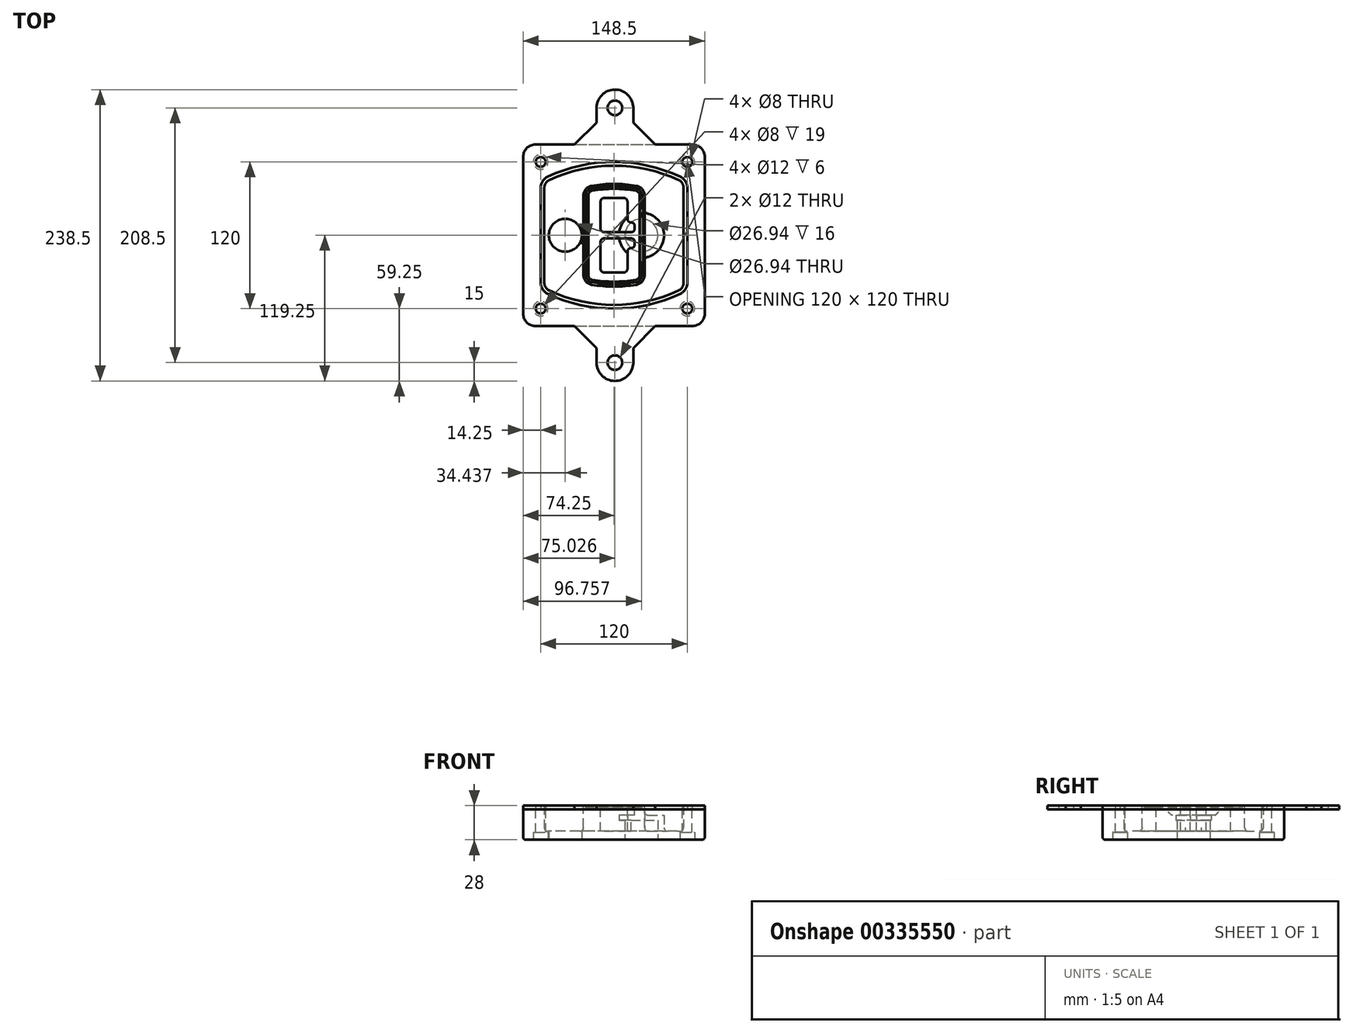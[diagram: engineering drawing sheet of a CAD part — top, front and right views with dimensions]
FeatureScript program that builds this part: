
annotation { "Feature Type Name" : "Feature", "Feature Type Description" : "" }
export const myFeature = defineFeature(function(context is Context, id is Id, definition is map)
    precondition{}
    {
        {
            var Q0;
            Q0=qCreatedBy(makeId("Top.planeOp"),FACE);
            var sketch = newSketch(context, id + "F0", { "sketchPlane" : qUnion([Q0])});
            skPoint(sketch, "E0.rect.middle", {"position": v(0, 0) * mm});
            skLineSegment(sketch, "E1.bottom", {"start": v(-64.25, -74.25) * mm, "end": v(64.25, -74.25) * mm});
            skLineSegment(sketch, "E1.top", {"start": v(-64.25, 74.25) * mm, "end": v(64.25, 74.25) * mm});
            skLineSegment(sketch, "E1.left", {"start": v(-74.25, -64.25) * mm, "end": v(-74.25, 64.25) * mm});
            skLineSegment(sketch, "E1.right", {"start": v(74.25, -64.25) * mm, "end": v(74.25, 64.25) * mm});
            skLineSegment(sketch, "E2", {"start": v(-74.25, 74.25) * mm, "end": v(74.25, -74.25) * mm, "construction": true});
            skLineSegment(sketch, "E3", {"start": v(74.25, 74.25) * mm, "end": v(-74.25, -74.25) * mm, "construction": true});
            skCircle(sketch, "E4", {"center": v(-60, 60) * mm, "radius": 4 * mm});
            skCircle(sketch, "E5", {"center": v(60, 60) * mm, "radius": 4 * mm});
            skCircle(sketch, "E6", {"center": v(60, -60) * mm, "radius": 4 * mm});
            skCircle(sketch, "E7", {"center": v(-60, -60) * mm, "radius": 4 * mm});
            skLineSegment(sketch, "E8", {"start": v(-60, 60) * mm, "end": v(60, 60) * mm, "construction": true});
            skLineSegment(sketch, "E9", {"start": v(60, 60) * mm, "end": v(60, -60) * mm, "construction": true});
            skLineSegment(sketch, "E10", {"start": v(60, -60) * mm, "end": v(-60, -60) * mm, "construction": true});
            skLineSegment(sketch, "E11", {"start": v(-60, -60) * mm, "end": v(-60, 60) * mm, "construction": true});
            skLineSegment(sketch, "E12", {"start": v(-60, 38.83) * mm, "end": v(-60, -38.83) * mm});
            skLineSegment(sketch, "E13", {"start": v(60, 38.83) * mm, "end": v(60, -38.83) * mm});
            skArc(sketch, "E14", {"start": v(54.26, 47.88) * mm, "mid": v(0, 60) * mm, "end": v(-54.26, 47.88) * mm});
            skArc(sketch, "E15", {"start": v(-54.26, -47.88) * mm, "mid": v(0, -60) * mm, "end": v(54.26, -47.88) * mm});
            skLineSegment(sketch, "E16", {"start": v(-60, 0) * mm, "end": v(60, 0) * mm, "construction": true});
            skPoint(sketch, "E17.visualSharp", {"position": v(-60, -45) * mm});
            skArc(sketch, "E17.filletArc", {"start": v(-60, -38.83) * mm, "mid": v(-58.44, -44.2) * mm, "end": v(-54.26, -47.88) * mm});
            skPoint(sketch, "E18.visualSharp", {"position": v(-60, 45) * mm});
            skArc(sketch, "E18.filletArc", {"start": v(-54.26, 47.88) * mm, "mid": v(-58.44, 44.2) * mm, "end": v(-60, 38.83) * mm});
            skPoint(sketch, "E19.visualSharp", {"position": v(60, 45) * mm});
            skArc(sketch, "E19.filletArc", {"start": v(60, 38.83) * mm, "mid": v(58.44, 44.2) * mm, "end": v(54.26, 47.88) * mm});
            skPoint(sketch, "E20.visualSharp", {"position": v(60, -45) * mm});
            skArc(sketch, "E20.filletArc", {"start": v(54.26, -47.88) * mm, "mid": v(58.44, -44.2) * mm, "end": v(60, -38.83) * mm});
            skPoint(sketch, "E21.visualSharp", {"position": v(-74.25, 74.25) * mm});
            skArc(sketch, "E21.filletArc", {"start": v(-64.25, 74.25) * mm, "mid": v(-71.32, 71.32) * mm, "end": v(-74.25, 64.25) * mm});
            skPoint(sketch, "E22.visualSharp", {"position": v(74.25, 74.25) * mm});
            skArc(sketch, "E22.filletArc", {"start": v(74.25, 64.25) * mm, "mid": v(71.32, 71.32) * mm, "end": v(64.25, 74.25) * mm});
            skPoint(sketch, "E23.visualSharp", {"position": v(74.25, -74.25) * mm});
            skArc(sketch, "E23.filletArc", {"start": v(64.25, -74.25) * mm, "mid": v(71.32, -71.32) * mm, "end": v(74.25, -64.25) * mm});
            skPoint(sketch, "E24.visualSharp", {"position": v(-74.25, -74.25) * mm});
            skArc(sketch, "E24.filletArc", {"start": v(-74.25, -64.25) * mm, "mid": v(-71.32, -71.32) * mm, "end": v(-64.25, -74.25) * mm});
            skArc(sketch, "E25.0", {"start": v(57, 38.83) * mm, "mid": v(55.9, 42.58) * mm, "end": v(52.98, 45.17) * mm});
            skLineSegment(sketch, "E25.1", {"start": v(57, 38.83) * mm, "end": v(57, -38.83) * mm});
            skArc(sketch, "E25.2", {"start": v(52.98, -45.17) * mm, "mid": v(55.9, -42.58) * mm, "end": v(57, -38.83) * mm});
            skArc(sketch, "E25.3", {"start": v(-52.98, -45.17) * mm, "mid": v(0, -57) * mm, "end": v(52.98, -45.17) * mm});
            skArc(sketch, "E25.4", {"start": v(-57, -38.83) * mm, "mid": v(-55.9, -42.58) * mm, "end": v(-52.98, -45.17) * mm});
            skArc(sketch, "E25.5", {"start": v(52.98, 45.17) * mm, "mid": v(0, 57) * mm, "end": v(-52.98, 45.17) * mm});
            skLineSegment(sketch, "E25.6", {"start": v(-57, 38.83) * mm, "end": v(-57, -38.83) * mm});
            skArc(sketch, "E25.7", {"start": v(-52.98, 45.17) * mm, "mid": v(-55.9, 42.58) * mm, "end": v(-57, 38.83) * mm});
            skArc(sketch, "E26.0", {"start": v(-55.96, 51.5) * mm, "mid": v(-61.82, 46.33) * mm, "end": v(-64, 38.83) * mm});
            skArc(sketch, "E26.1", {"start": v(55.96, 51.5) * mm, "mid": v(0, 64) * mm, "end": v(-55.96, 51.5) * mm});
            skArc(sketch, "E26.2", {"start": v(64, 38.83) * mm, "mid": v(61.82, 46.33) * mm, "end": v(55.96, 51.5) * mm});
            skLineSegment(sketch, "E26.3", {"start": v(64, 38.83) * mm, "end": v(64, -38.83) * mm});
            skArc(sketch, "E26.4", {"start": v(55.96, -51.5) * mm, "mid": v(61.82, -46.33) * mm, "end": v(64, -38.83) * mm});
            skLineSegment(sketch, "E26.5", {"start": v(-64, 38.83) * mm, "end": v(-64, -38.83) * mm});
            skArc(sketch, "E26.6", {"start": v(-55.96, -51.5) * mm, "mid": v(0, -64) * mm, "end": v(55.96, -51.5) * mm});
            skArc(sketch, "E26.7", {"start": v(-64, -38.83) * mm, "mid": v(-61.82, -46.33) * mm, "end": v(-55.96, -51.5) * mm});
            skSolve(sketch);
        }
        {
            var Q0;
            Q0=makeQuery(id+"F0.imprint","IMPRINT",FACE,{"disambiguationData":[TD([[makeQuery(id+"F0.imprint","IMPRINT",EDGE,{"derivedFrom":sQuery(id+"F0.wireOp",EDGE,"E1.bottom")}),1.0]])]});
            var Q1;
            Q1=makeQuery(id+"F0.imprint","IMPRINT",FACE,{"disambiguationData":[TD([[makeQuery(id+"F0.imprint","IMPRINT",EDGE,{"derivedFrom":sQuery(id+"F0.wireOp",EDGE,"E12")}),1.0]])]});
            var Q2;
            Q2=makeQuery(id+"F0.imprint","IMPRINT",FACE,{"disambiguationData":[TD([[makeQuery(id+"F0.imprint","IMPRINT",EDGE,{"derivedFrom":sQuery(id+"F0.wireOp",EDGE,"E25.0")}),1.0]])]});
            var Q3;
            Q3=makeQuery(id+"F0.imprint","IMPRINT",FACE,{"disambiguationData":[TD([[makeQuery(id+"F0.imprint","IMPRINT",EDGE,{"derivedFrom":sQuery(id+"F0.wireOp",EDGE,"E12")}),-1.0]])]});
            extrude(context, id + "F1", {"entities" : qUnion([Q0, Q1, Q2, Q3]), "oppositeDirection" : true, "depth" : 25 * mm});
        }
        {
            var Q0;
            Q0=makeQuery(id+"F0.imprint","IMPRINT",FACE,{"disambiguationData":[TD([[makeQuery(id+"F0.imprint","IMPRINT",EDGE,{"derivedFrom":sQuery(id+"F0.wireOp",EDGE,"E12")}),1.0]])]});
            extrude(context, id + "F2", {"entities" : qUnion([Q0]), "operationType" : NewBodyOperationType.ADD, "depth" : 3 * mm});
        }
        {
            var Q0;
            Q0=makeQuery(id+"F0.imprint","IMPRINT",FACE,{"disambiguationData":[TD([[makeQuery(id+"F0.imprint","IMPRINT",EDGE,{"derivedFrom":sQuery(id+"F0.wireOp",EDGE,"E25.0")}),1.0]])]});
            extrude(context, id + "F3", {"entities" : qUnion([Q0]), "operationType" : NewBodyOperationType.REMOVE, "oppositeDirection" : true, "depth" : 18 * mm});
        }
        {
            var Q0;
            Q0=makeQuery(id+"F2.opExtrude","CAP_FACE",FACE,{"disambiguationData":[OSD([sQuery(id+"F0.wireOp",EDGE,"E12"),sQuery(id+"F0.wireOp",EDGE,"E13"),sQuery(id+"F0.wireOp",EDGE,"E14"),sQuery(id+"F0.wireOp",EDGE,"E15"),sQuery(id+"F0.wireOp",EDGE,"E17.filletArc"),sQuery(id+"F0.wireOp",EDGE,"E18.filletArc"),sQuery(id+"F0.wireOp",EDGE,"E19.filletArc"),sQuery(id+"F0.wireOp",EDGE,"E20.filletArc"),sQuery(id+"F0.wireOp",EDGE,"E25.0"),sQuery(id+"F0.wireOp",EDGE,"E25.1"),sQuery(id+"F0.wireOp",EDGE,"E25.2"),sQuery(id+"F0.wireOp",EDGE,"E25.3"),sQuery(id+"F0.wireOp",EDGE,"E25.4"),sQuery(id+"F0.wireOp",EDGE,"E25.5"),sQuery(id+"F0.wireOp",EDGE,"E25.6"),sQuery(id+"F0.wireOp",EDGE,"E25.7")])],"isStart":false});
            var sketch = newSketch(context, id + "F4", { "sketchPlane" : qUnion([Q0])});
            skArc(sketch, "E27.0", {"start": v(-18.34, -40.45) * mm, "mid": v(0, -42) * mm, "end": v(18.34, -40.45) * mm});
            skArc(sketch, "E28.0", {"start": v(18.34, 40.45) * mm, "mid": v(0, 42) * mm, "end": v(-18.34, 40.45) * mm});
            skLineSegment(sketch, "E29", {"start": v(-25, 32.57) * mm, "end": v(-25, -32.57) * mm});
            skLineSegment(sketch, "E30", {"start": v(25, 32.57) * mm, "end": v(25, -32.57) * mm});
            skLineSegment(sketch, "E31", {"start": v(-25, 39.1) * mm, "end": v(25, 39.1) * mm, "construction": true});
            skLineSegment(sketch, "E32", {"start": v(-25, -39.1) * mm, "end": v(25, -39.1) * mm, "construction": true});
            skPoint(sketch, "E33.visualSharp", {"position": v(-25, 39.1) * mm});
            skArc(sketch, "E33.filletArc", {"start": v(-18.34, 40.45) * mm, "mid": v(-23.11, 37.73) * mm, "end": v(-25, 32.57) * mm});
            skPoint(sketch, "E34.visualSharp", {"position": v(25, 39.1) * mm});
            skArc(sketch, "E34.filletArc", {"start": v(25, 32.57) * mm, "mid": v(23.11, 37.73) * mm, "end": v(18.34, 40.45) * mm});
            skPoint(sketch, "E35.visualSharp", {"position": v(25, -39.1) * mm});
            skArc(sketch, "E35.filletArc", {"start": v(18.34, -40.45) * mm, "mid": v(23.11, -37.73) * mm, "end": v(25, -32.57) * mm});
            skPoint(sketch, "E36.visualSharp", {"position": v(-25, -39.1) * mm});
            skArc(sketch, "E36.filletArc", {"start": v(-25, -32.57) * mm, "mid": v(-23.11, -37.73) * mm, "end": v(-18.34, -40.45) * mm});
            skArc(sketch, "E37.0", {"start": v(52.98, 45.17) * mm, "mid": v(0, 57) * mm, "end": v(-52.98, 45.17) * mm});
            skArc(sketch, "E37.1", {"start": v(-52.98, 45.17) * mm, "mid": v(-55.9, 42.58) * mm, "end": v(-57, 38.83) * mm});
            skLineSegment(sketch, "E37.2", {"start": v(-57, 38.83) * mm, "end": v(-57, -38.83) * mm});
            skArc(sketch, "E37.3", {"start": v(-57, -38.83) * mm, "mid": v(-55.9, -42.58) * mm, "end": v(-52.98, -45.17) * mm});
            skArc(sketch, "E37.4", {"start": v(-52.98, -45.17) * mm, "mid": v(0, -57) * mm, "end": v(52.98, -45.17) * mm});
            skArc(sketch, "E37.5", {"start": v(52.98, -45.17) * mm, "mid": v(55.9, -42.58) * mm, "end": v(57, -38.83) * mm});
            skLineSegment(sketch, "E37.6", {"start": v(57, 38.83) * mm, "end": v(57, -38.83) * mm});
            skArc(sketch, "E37.7", {"start": v(57, 38.83) * mm, "mid": v(55.9, 42.58) * mm, "end": v(52.98, 45.17) * mm});
            skLineSegment(sketch, "E38.0", {"start": v(23, 32.57) * mm, "end": v(23, -32.57) * mm});
            skArc(sketch, "E38.1", {"start": v(18, -38.48) * mm, "mid": v(21.58, -36.44) * mm, "end": v(23, -32.57) * mm});
            skArc(sketch, "E38.2", {"start": v(-18, -38.48) * mm, "mid": v(0, -40) * mm, "end": v(18, -38.48) * mm});
            skArc(sketch, "E38.3", {"start": v(-23, -32.57) * mm, "mid": v(-21.58, -36.44) * mm, "end": v(-18, -38.48) * mm});
            skLineSegment(sketch, "E38.4", {"start": v(-23, 32.57) * mm, "end": v(-23, -32.57) * mm});
            skArc(sketch, "E38.5", {"start": v(23, 32.57) * mm, "mid": v(21.58, 36.44) * mm, "end": v(18, 38.48) * mm});
            skArc(sketch, "E38.6", {"start": v(-18, 38.48) * mm, "mid": v(-21.58, 36.44) * mm, "end": v(-23, 32.57) * mm});
            skArc(sketch, "E38.7", {"start": v(18, 38.48) * mm, "mid": v(0, 40) * mm, "end": v(-18, 38.48) * mm});
            skArc(sketch, "E39.0", {"start": v(21, 32.57) * mm, "mid": v(20.06, 35.15) * mm, "end": v(17.67, 36.5) * mm});
            skLineSegment(sketch, "E39.1", {"start": v(21, 32.57) * mm, "end": v(21, -32.57) * mm});
            skArc(sketch, "E39.2", {"start": v(17.67, -36.5) * mm, "mid": v(20.06, -35.15) * mm, "end": v(21, -32.57) * mm});
            skArc(sketch, "E39.3", {"start": v(-17.67, -36.5) * mm, "mid": v(0, -38) * mm, "end": v(17.67, -36.5) * mm});
            skArc(sketch, "E39.4", {"start": v(-21, -32.57) * mm, "mid": v(-20.06, -35.15) * mm, "end": v(-17.67, -36.5) * mm});
            skArc(sketch, "E39.5", {"start": v(17.67, 36.5) * mm, "mid": v(0, 38) * mm, "end": v(-17.67, 36.5) * mm});
            skLineSegment(sketch, "E39.6", {"start": v(-21, 32.57) * mm, "end": v(-21, -32.57) * mm});
            skArc(sketch, "E39.7", {"start": v(-17.67, 36.5) * mm, "mid": v(-20.06, 35.15) * mm, "end": v(-21, 32.57) * mm});
            skLineSegment(sketch, "E40", {"start": v(-25, 0) * mm, "end": v(25, 0) * mm, "construction": true});
            skLineSegment(sketch, "E41", {"start": v(-11, 5.5) * mm, "end": v(-11, 27.5) * mm});
            skLineSegment(sketch, "E42", {"start": v(-8, 30.5) * mm, "end": v(8, 30.5) * mm});
            skLineSegment(sketch, "E43", {"start": v(11, 27.5) * mm, "end": v(11, 13.5) * mm});
            skLineSegment(sketch, "E44", {"start": v(14, 10.5) * mm, "end": v(14, 10.5) * mm});
            skLineSegment(sketch, "E45", {"start": v(17, 7.5) * mm, "end": v(17, 5.5) * mm});
            skLineSegment(sketch, "E46", {"start": v(14, 2.5) * mm, "end": v(-8, 2.5) * mm});
            skPoint(sketch, "E47.visualSharp", {"position": v(-11, 30.5) * mm});
            skArc(sketch, "E47.filletArc", {"start": v(-8, 30.5) * mm, "mid": v(-10.12, 29.62) * mm, "end": v(-11, 27.5) * mm});
            skPoint(sketch, "E48.visualSharp", {"position": v(11, 30.5) * mm});
            skArc(sketch, "E48.filletArc", {"start": v(11, 27.5) * mm, "mid": v(10.12, 29.62) * mm, "end": v(8, 30.5) * mm});
            skPoint(sketch, "E49.visualSharp", {"position": v(11, 10.5) * mm});
            skArc(sketch, "E49.filletArc", {"start": v(11, 13.5) * mm, "mid": v(11.88, 11.38) * mm, "end": v(14, 10.5) * mm});
            skPoint(sketch, "E50.visualSharp", {"position": v(17, 10.5) * mm});
            skArc(sketch, "E50.filletArc", {"start": v(17, 7.5) * mm, "mid": v(16.12, 9.62) * mm, "end": v(14, 10.5) * mm});
            skPoint(sketch, "E51.visualSharp", {"position": v(17, 2.5) * mm});
            skArc(sketch, "E51.filletArc", {"start": v(14, 2.5) * mm, "mid": v(16.12, 3.38) * mm, "end": v(17, 5.5) * mm});
            skPoint(sketch, "E52.visualSharp", {"position": v(-11, 2.5) * mm});
            skArc(sketch, "E52.filletArc", {"start": v(-11, 5.5) * mm, "mid": v(-10.12, 3.38) * mm, "end": v(-8, 2.5) * mm});
            skLineSegment(sketch, "E53.0.MirrorCS", {"start": v(14, -2.5) * mm, "end": v(-8, -2.5) * mm});
            skArc(sketch, "E54.0.MirrorCS", {"start": v(-11, -5.5) * mm, "mid": v(-10.12, -3.38) * mm, "end": v(-8, -2.5) * mm});
            skLineSegment(sketch, "E55.0.MirrorCS", {"start": v(-11, -5.5) * mm, "end": v(-11, -27.5) * mm});
            skArc(sketch, "E56.0.MirrorCS", {"start": v(-8, -30.5) * mm, "mid": v(-10.12, -29.62) * mm, "end": v(-11, -27.5) * mm});
            skLineSegment(sketch, "E57.0.MirrorCS", {"start": v(-8, -30.5) * mm, "end": v(8, -30.5) * mm});
            skArc(sketch, "E58.0.MirrorCS", {"start": v(11, -27.5) * mm, "mid": v(10.12, -29.62) * mm, "end": v(8, -30.5) * mm});
            skLineSegment(sketch, "E59.0.MirrorCS", {"start": v(11, -27.5) * mm, "end": v(11, -13.5) * mm});
            skArc(sketch, "E60.0.MirrorCS", {"start": v(11, -13.5) * mm, "mid": v(11.88, -11.38) * mm, "end": v(14, -10.5) * mm});
            skArc(sketch, "E61.0.MirrorCS", {"start": v(17, -7.5) * mm, "mid": v(16.12, -9.62) * mm, "end": v(14, -10.5) * mm});
            skLineSegment(sketch, "E62.0.MirrorCS", {"start": v(17, -7.5) * mm, "end": v(17, -5.5) * mm});
            skArc(sketch, "E63.0.MirrorCS", {"start": v(14, -2.5) * mm, "mid": v(16.12, -3.38) * mm, "end": v(17, -5.5) * mm});
            skSolve(sketch);
        }
        {
            var Q0;
            Q0=makeQuery(id+"F4.imprint","IMPRINT",FACE,{"disambiguationData":[TD([[makeQuery(id+"F4.imprint","IMPRINT",EDGE,{"derivedFrom":sQuery(id+"F4.wireOp",EDGE,"E27.0")}),1.0]])]});
            var Q1;
            Q1=makeQuery(id+"F4.imprint","IMPRINT",FACE,{"disambiguationData":[TD([[makeQuery(id+"F4.imprint","IMPRINT",EDGE,{"derivedFrom":sQuery(id+"F4.wireOp",EDGE,"E38.0")}),-1.0]])]});
            var Q2;
            Q2=makeQuery(id+"F4.imprint","IMPRINT",FACE,{"disambiguationData":[TD([[makeQuery(id+"F4.imprint","IMPRINT",EDGE,{"derivedFrom":sQuery(id+"F4.wireOp",EDGE,"E39.0")}),1.0]])]});
            extrude(context, id + "F5", {"entities" : qUnion([Q0, Q1, Q2]), "operationType" : NewBodyOperationType.ADD, "endBound" : BoundingType.UP_TO_NEXT, "oppositeDirection" : true, "depth" : 25 * mm});
        }
        {
            var Q0;
            Q0=makeQuery(id+"F4.imprint","IMPRINT",FACE,{"disambiguationData":[TD([[makeQuery(id+"F4.imprint","IMPRINT",EDGE,{"derivedFrom":sQuery(id+"F4.wireOp",EDGE,"E38.0")}),-1.0]])]});
            extrude(context, id + "F6", {"entities" : qUnion([Q0]), "operationType" : NewBodyOperationType.REMOVE, "oppositeDirection" : true, "depth" : 2 * mm});
        }
        {
            var Q0;
            Q0=makeQuery(id+"F1.opExtrude","CAP_FACE",FACE,{"disambiguationData":[OSD([sQuery(id+"F0.wireOp",EDGE,"E1.bottom"),sQuery(id+"F0.wireOp",EDGE,"E1.top"),sQuery(id+"F0.wireOp",EDGE,"E1.left"),sQuery(id+"F0.wireOp",EDGE,"E1.right"),sQuery(id+"F0.wireOp",EDGE,"E4"),sQuery(id+"F0.wireOp",EDGE,"E5"),sQuery(id+"F0.wireOp",EDGE,"E6"),sQuery(id+"F0.wireOp",EDGE,"E7"),sQuery(id+"F0.wireOp",EDGE,"E21.filletArc"),sQuery(id+"F0.wireOp",EDGE,"E22.filletArc"),sQuery(id+"F0.wireOp",EDGE,"E23.filletArc"),sQuery(id+"F0.wireOp",EDGE,"E24.filletArc")])],"isStart":false});
            var sketch = newSketch(context, id + "F7", { "sketchPlane" : qUnion([Q0])});
            skCircle(sketch, "E64", {"center": v(22.5, 0) * mm, "radius": 13.47 * mm});
            skCircle(sketch, "E65", {"center": v(-39.81, 0) * mm, "radius": 13.47 * mm});
            skLineSegment(sketch, "E66", {"start": v(74.25, 0) * mm, "end": v(-74.25, 0) * mm});
            skCircle(sketch, "E67", {"center": v(22.5, 0) * mm, "radius": 18.47 * mm});
            skCircle(sketch, "E68", {"center": v(60, -60) * mm, "radius": 6 * mm});
            skCircle(sketch, "E69", {"center": v(-60, -60) * mm, "radius": 6 * mm});
            skCircle(sketch, "E70", {"center": v(-60, 60) * mm, "radius": 6 * mm});
            skCircle(sketch, "E71", {"center": v(60, 60) * mm, "radius": 6 * mm});
            skSolve(sketch);
        }
        {
            var Q0;
            {var subQ1=sQuery(id+"F7.wireOp",EDGE,"E66");var subQ4=sQuery(id+"F7.wireOp",EDGE,"E64");var subQ6=makeQuery(id+"F7.imprint","INTERSECT",VERTEX,{"disambiguationData":[OD(0.0)],"derivedFrom":[subQ4,subQ1]});Q0=makeQuery(id+"F7.imprint","IMPRINT",FACE,{"disambiguationData":[TD([[makeQuery(id+"F7.imprint","IMPRINT",EDGE,{"disambiguationData":[TD([[subQ6,-1.0]])],"derivedFrom":subQ4}),-1.0]])]});}
            var Q1;
            {var subQ0=sQuery(id+"F7.wireOp",EDGE,"E66");var subQ1=sQuery(id+"F7.wireOp",EDGE,"E64");var subQ3=makeQuery(id+"F7.imprint","INTERSECT",VERTEX,{"disambiguationData":[OD(0.0)],"derivedFrom":[subQ1,subQ0]});Q1=makeQuery(id+"F7.imprint","IMPRINT",FACE,{"disambiguationData":[TD([[makeQuery(id+"F7.imprint","IMPRINT",EDGE,{"disambiguationData":[TD([[subQ3,-1.0]])],"derivedFrom":subQ1}),1.0]])]});}
            var Q2;
            {var subQ0=sQuery(id+"F7.wireOp",EDGE,"E66");var subQ1=sQuery(id+"F7.wireOp",EDGE,"E64");var subQ3=makeQuery(id+"F7.imprint","INTERSECT",VERTEX,{"disambiguationData":[OD(0.0)],"derivedFrom":[subQ1,subQ0]});Q2=makeQuery(id+"F7.imprint","IMPRINT",FACE,{"disambiguationData":[TD([[makeQuery(id+"F7.imprint","IMPRINT",EDGE,{"disambiguationData":[TD([[subQ3,1.0]])],"derivedFrom":subQ1}),1.0]])]});}
            var Q3;
            {var subQ1=sQuery(id+"F7.wireOp",EDGE,"E66");var subQ4=sQuery(id+"F7.wireOp",EDGE,"E64");var subQ6=makeQuery(id+"F7.imprint","INTERSECT",VERTEX,{"disambiguationData":[OD(0.0)],"derivedFrom":[subQ4,subQ1]});Q3=makeQuery(id+"F7.imprint","IMPRINT",FACE,{"disambiguationData":[TD([[makeQuery(id+"F7.imprint","IMPRINT",EDGE,{"disambiguationData":[TD([[subQ6,1.0]])],"derivedFrom":subQ4}),-1.0]])]});}
            extrude(context, id + "F8", {"entities" : qUnion([Q0, Q1, Q2, Q3]), "operationType" : NewBodyOperationType.ADD, "oppositeDirection" : true, "depth" : 20 * mm});
        }
        {
            var Q0;
            {var subQ0=sQuery(id+"F7.wireOp",EDGE,"E66");var subQ1=sQuery(id+"F7.wireOp",EDGE,"E64");var subQ3=makeQuery(id+"F7.imprint","INTERSECT",VERTEX,{"disambiguationData":[OD(0.0)],"derivedFrom":[subQ1,subQ0]});Q0=makeQuery(id+"F7.imprint","IMPRINT",FACE,{"disambiguationData":[TD([[makeQuery(id+"F7.imprint","IMPRINT",EDGE,{"disambiguationData":[TD([[subQ3,-1.0]])],"derivedFrom":subQ1}),1.0]])]});}
            var Q1;
            {var subQ0=sQuery(id+"F7.wireOp",EDGE,"E66");var subQ1=sQuery(id+"F7.wireOp",EDGE,"E64");var subQ3=makeQuery(id+"F7.imprint","INTERSECT",VERTEX,{"disambiguationData":[OD(0.0)],"derivedFrom":[subQ1,subQ0]});Q1=makeQuery(id+"F7.imprint","IMPRINT",FACE,{"disambiguationData":[TD([[makeQuery(id+"F7.imprint","IMPRINT",EDGE,{"disambiguationData":[TD([[subQ3,1.0]])],"derivedFrom":subQ1}),1.0]])]});}
            extrude(context, id + "F9", {"entities" : qUnion([Q0, Q1]), "operationType" : NewBodyOperationType.REMOVE, "oppositeDirection" : true, "depth" : 16 * mm});
        }
        {
            var Q0;
            {var subQ0=sQuery(id+"F7.wireOp",EDGE,"E66");var subQ1=sQuery(id+"F7.wireOp",EDGE,"E65");var subQ3=makeQuery(id+"F7.imprint","INTERSECT",VERTEX,{"disambiguationData":[OD(0.0)],"derivedFrom":[subQ1,subQ0]});Q0=makeQuery(id+"F7.imprint","IMPRINT",FACE,{"disambiguationData":[TD([[makeQuery(id+"F7.imprint","IMPRINT",EDGE,{"disambiguationData":[TD([[subQ3,-1.0]])],"derivedFrom":subQ1}),1.0]])]});}
            var Q1;
            {var subQ0=sQuery(id+"F7.wireOp",EDGE,"E66");var subQ1=sQuery(id+"F7.wireOp",EDGE,"E65");var subQ3=makeQuery(id+"F7.imprint","INTERSECT",VERTEX,{"disambiguationData":[OD(0.0)],"derivedFrom":[subQ1,subQ0]});Q1=makeQuery(id+"F7.imprint","IMPRINT",FACE,{"disambiguationData":[TD([[makeQuery(id+"F7.imprint","IMPRINT",EDGE,{"disambiguationData":[TD([[subQ3,1.0]])],"derivedFrom":subQ1}),1.0]])]});}
            extrude(context, id + "F10", {"entities" : qUnion([Q0, Q1]), "operationType" : NewBodyOperationType.REMOVE, "oppositeDirection" : true, "depth" : 25 * mm});
        }
        {
            var Q0;
            Q0=makeQuery(id+"F7.imprint","IMPRINT",FACE,{"disambiguationData":[TD([[makeQuery(id+"F7.imprint","IMPRINT",EDGE,{"derivedFrom":sQuery(id+"F7.wireOp",EDGE,"E68")}),1.0]])]});
            var Q1;
            Q1=makeQuery(id+"F7.imprint","IMPRINT",FACE,{"disambiguationData":[TD([[makeQuery(id+"F7.imprint","IMPRINT",EDGE,{"derivedFrom":makeQuery(id+"F1.opExtrude","CAP_EDGE",EDGE,{"disambiguationData":[OSD([sQuery(id+"F0.wireOp",EDGE,"E5")])],"isStart":false})}),-1.0]])]});
            var Q2;
            Q2=makeQuery(id+"F7.imprint","IMPRINT",FACE,{"disambiguationData":[TD([[makeQuery(id+"F7.imprint","IMPRINT",EDGE,{"derivedFrom":sQuery(id+"F7.wireOp",EDGE,"E69")}),1.0]])]});
            var Q3;
            Q3=makeQuery(id+"F7.imprint","IMPRINT",FACE,{"disambiguationData":[TD([[makeQuery(id+"F7.imprint","IMPRINT",EDGE,{"derivedFrom":makeQuery(id+"F1.opExtrude","CAP_EDGE",EDGE,{"disambiguationData":[OSD([sQuery(id+"F0.wireOp",EDGE,"E4")])],"isStart":false})}),-1.0]])]});
            var Q4;
            Q4=makeQuery(id+"F7.imprint","IMPRINT",FACE,{"disambiguationData":[TD([[makeQuery(id+"F7.imprint","IMPRINT",EDGE,{"derivedFrom":sQuery(id+"F7.wireOp",EDGE,"E70")}),1.0]])]});
            var Q5;
            Q5=makeQuery(id+"F7.imprint","IMPRINT",FACE,{"disambiguationData":[TD([[makeQuery(id+"F7.imprint","IMPRINT",EDGE,{"derivedFrom":makeQuery(id+"F1.opExtrude","CAP_EDGE",EDGE,{"disambiguationData":[OSD([sQuery(id+"F0.wireOp",EDGE,"E7")])],"isStart":false})}),-1.0]])]});
            var Q6;
            Q6=makeQuery(id+"F7.imprint","IMPRINT",FACE,{"disambiguationData":[TD([[makeQuery(id+"F7.imprint","IMPRINT",EDGE,{"derivedFrom":sQuery(id+"F7.wireOp",EDGE,"E71")}),1.0]])]});
            var Q7;
            Q7=makeQuery(id+"F7.imprint","IMPRINT",FACE,{"disambiguationData":[TD([[makeQuery(id+"F7.imprint","IMPRINT",EDGE,{"derivedFrom":makeQuery(id+"F1.opExtrude","CAP_EDGE",EDGE,{"disambiguationData":[OSD([sQuery(id+"F0.wireOp",EDGE,"E6")])],"isStart":false})}),-1.0]])]});
            extrude(context, id + "F11", {"entities" : qUnion([Q0, Q1, Q2, Q3, Q4, Q5, Q6, Q7]), "operationType" : NewBodyOperationType.REMOVE, "oppositeDirection" : true, "depth" : 6 * mm});
        }
        {
            var Q0;
            Q0=makeQuery(id+"F9.boolean.opBoolean","COPY",FACE,{"derivedFrom":makeQuery(id+"F9.opExtrude","CAP_FACE",FACE,{"disambiguationData":[OSD([sQuery(id+"F7.wireOp",EDGE,"E64")])],"isStart":false})});
            var sketch = newSketch(context, id + "F12", { "sketchPlane" : qUnion([Q0])});
            skArc(sketch, "E72.0", {"start": v(11, 14.45) * mm, "mid": v(6.45, 9.13) * mm, "end": v(4.2, 2.5) * mm});
            skArc(sketch, "E72.1", {"start": v(4.2, -2.5) * mm, "mid": v(6.45, -9.13) * mm, "end": v(11, -14.45) * mm});
            skLineSegment(sketch, "E73", {"start": v(4.2, -2.5) * mm, "end": v(14, -2.5) * mm});
            skLineSegment(sketch, "E74.0", {"start": v(14, 2.5) * mm, "end": v(4.2, 2.5) * mm});
            skArc(sketch, "E74.1", {"start": v(14, 2.5) * mm, "mid": v(16.12, 3.38) * mm, "end": v(17, 5.5) * mm});
            skLineSegment(sketch, "E74.2", {"start": v(17, 7.5) * mm, "end": v(17, 5.5) * mm});
            skArc(sketch, "E74.3", {"start": v(17, 7.5) * mm, "mid": v(16.12, 9.62) * mm, "end": v(14, 10.5) * mm});
            skArc(sketch, "E74.4", {"start": v(11, 13.5) * mm, "mid": v(11.88, 11.38) * mm, "end": v(14, 10.5) * mm});
            skLineSegment(sketch, "E74.5", {"start": v(11, 14.45) * mm, "end": v(11, 13.5) * mm});
            skLineSegment(sketch, "E74.7", {"start": v(14, -2.5) * mm, "end": v(4.2, -2.5) * mm});
            skArc(sketch, "E74.8", {"start": v(14, -2.5) * mm, "mid": v(16.12, -3.38) * mm, "end": v(17, -5.5) * mm});
            skLineSegment(sketch, "E74.9", {"start": v(17, -7.5) * mm, "end": v(17, -5.5) * mm});
            skArc(sketch, "E74.10", {"start": v(17, -7.5) * mm, "mid": v(16.12, -9.62) * mm, "end": v(14, -10.5) * mm});
            skArc(sketch, "E74.11", {"start": v(11, -13.5) * mm, "mid": v(11.88, -11.38) * mm, "end": v(14, -10.5) * mm});
            skLineSegment(sketch, "E74.12", {"start": v(11, -14.45) * mm, "end": v(11, -13.5) * mm});
            skPoint(sketch, "E75.orphan", {"position": v(11, -27.5) * mm});
            skPoint(sketch, "E76.orphan", {"position": v(-8, -2.5) * mm});
            skPoint(sketch, "E77.orphan", {"position": v(-8, 2.5) * mm});
            skPoint(sketch, "E78.orphan", {"position": v(11, 27.5) * mm});
            skSolve(sketch);
        }
        {
            var Q0;
            {var subQ7=sQuery(id+"F12.wireOp",EDGE,"E72.0");var subQ14=sQuery(id+"F12.wireOp",EDGE,"E72.1");var subQ16=sQuery(id+"F12.wireOp",EDGE,"E74.1");var subQ18=sQuery(id+"F12.wireOp",EDGE,"E74.8");Q0=qUnion([makeQuery(id+"F12.imprint","IMPRINT",FACE,{"disambiguationData":[TD([[makeQuery(id+"F12.imprint","IMPRINT",EDGE,{"derivedFrom":subQ7}),1.0]])]}),makeQuery(id+"F12.imprint","IMPRINT",FACE,{"disambiguationData":[TD([[makeQuery(id+"F12.imprint","IMPRINT",EDGE,{"derivedFrom":subQ14}),1.0]])]}),makeQuery(id+"F12.imprint","IMPRINT",FACE,{"disambiguationData":[TD([[makeQuery(id+"F12.imprint","IMPRINT",EDGE,{"derivedFrom":subQ16}),1.0]])]}),makeQuery(id+"F12.imprint","IMPRINT",FACE,{"disambiguationData":[TD([[makeQuery(id+"F12.imprint","IMPRINT",EDGE,{"derivedFrom":subQ18}),-1.0]])]})]);}
            var Q1;
            Q1=makeQuery(id+"F5.boolean.opBoolean","SPLIT",FACE,{"disambiguationData":[TD([makeQuery(id+"F5.opExtrude","SWEPT_FACE",FACE,{"disambiguationData":[OSD([sQuery(id+"F4.wireOp",EDGE,"E41")])]})])],"derivedFrom":makeQuery(id+"F3.boolean.opBoolean","COPY",FACE,{"derivedFrom":makeQuery(id+"F3.opExtrude","CAP_FACE",FACE,{"disambiguationData":[OSD([sQuery(id+"F0.wireOp",EDGE,"E25.0"),sQuery(id+"F0.wireOp",EDGE,"E25.1"),sQuery(id+"F0.wireOp",EDGE,"E25.2"),sQuery(id+"F0.wireOp",EDGE,"E25.3"),sQuery(id+"F0.wireOp",EDGE,"E25.4"),sQuery(id+"F0.wireOp",EDGE,"E25.5"),sQuery(id+"F0.wireOp",EDGE,"E25.6"),sQuery(id+"F0.wireOp",EDGE,"E25.7")])],"isStart":false})})});
            extrude(context, id + "F13", {"entities" : qUnion([Q0]), "operationType" : NewBodyOperationType.REMOVE, "endBound" : BoundingType.UP_TO_SURFACE, "endBoundEntityFace" : qUnion([Q1]), "depth" : 25 * mm});
        }
        {
            var Q0;
            Q0=makeQuery(id+"F3.boolean.opBoolean","COPY",EDGE,{"derivedFrom":makeQuery(id+"F3.opExtrude","CAP_EDGE",EDGE,{"disambiguationData":[OSD([sQuery(id+"F0.wireOp",EDGE,"E25.6")])],"isStart":false})});
            var Q1;
            Q1=makeQuery(id+"F8.boolean.opBoolean","INTERSECT",EDGE,{"derivedFrom":[makeQuery(id+"F5.opExtrude","SWEPT_FACE",FACE,{"disambiguationData":[OSD([sQuery(id+"F4.wireOp",EDGE,"E30")])]}),makeQuery(id+"F8.opExtrude","CAP_FACE",FACE,{"disambiguationData":[OSD([sQuery(id+"F7.wireOp",EDGE,"E67")])],"isStart":false})]});
            var Q2;
            Q2=makeQuery(id+"F8.boolean.opBoolean","INTERSECT",EDGE,{"disambiguationData":[OD(1.0)],"derivedFrom":[makeQuery(id+"F5.opExtrude","SWEPT_FACE",FACE,{"disambiguationData":[OSD([sQuery(id+"F4.wireOp",EDGE,"E30")])]}),makeQuery(id+"F8.opExtrude","SWEPT_FACE",FACE,{"disambiguationData":[OSD([sQuery(id+"F7.wireOp",EDGE,"E67")])]})]});
            var Q3;
            {var subQ0=sQuery(id+"F4.wireOp",EDGE,"E30");Q3=makeQuery(id+"F8.boolean.opBoolean","SPLIT",EDGE,{"disambiguationData":[TD([makeQuery(id+"F5.opExtrude","SWEPT_FACE",FACE,{"disambiguationData":[OSD([sQuery(id+"F4.wireOp",EDGE,"E35.filletArc")])]})])],"derivedFrom":makeQuery(id+"F5.opExtrude","CAP_EDGE",EDGE,{"disambiguationData":[OSD([subQ0])],"isStart":false})});}
            var Q4;
            {var subQ0=sQuery(id+"F0.wireOp",EDGE,"E25.7");var subQ1=sQuery(id+"F0.wireOp",EDGE,"E25.1");var subQ2=sQuery(id+"F0.wireOp",EDGE,"E25.6");var subQ3=sQuery(id+"F0.wireOp",EDGE,"E25.5");var subQ4=sQuery(id+"F0.wireOp",EDGE,"E25.4");var subQ5=sQuery(id+"F0.wireOp",EDGE,"E25.0");var subQ6=sQuery(id+"F0.wireOp",EDGE,"E25.2");var subQ7=sQuery(id+"F0.wireOp",EDGE,"E25.3");Q4=makeQuery(id+"F8.boolean.opBoolean","INTERSECT",EDGE,{"derivedFrom":[makeQuery(id+"F5.boolean.opBoolean","SPLIT",FACE,{"disambiguationData":[TD([makeQuery(id+"F2.opExtrude","SWEPT_FACE",FACE,{"disambiguationData":[OSD([subQ5])]})])],"derivedFrom":makeQuery(id+"F3.boolean.opBoolean","COPY",FACE,{"derivedFrom":makeQuery(id+"F3.opExtrude","CAP_FACE",FACE,{"disambiguationData":[OSD([subQ5,subQ1,subQ6,subQ7,subQ4,subQ3,subQ2,subQ0])],"isStart":false})})}),makeQuery(id+"F8.opExtrude","SWEPT_FACE",FACE,{"disambiguationData":[OSD([sQuery(id+"F7.wireOp",EDGE,"E67")])]})]});}
            var Q5;
            Q5=makeQuery(id+"F8.boolean.opBoolean","INTERSECT",EDGE,{"disambiguationData":[OD(0.0)],"derivedFrom":[makeQuery(id+"F5.opExtrude","SWEPT_FACE",FACE,{"disambiguationData":[OSD([sQuery(id+"F4.wireOp",EDGE,"E30")])]}),makeQuery(id+"F8.opExtrude","SWEPT_FACE",FACE,{"disambiguationData":[OSD([sQuery(id+"F7.wireOp",EDGE,"E67")])]})]});
            fillet(context, id + "F14", {"entities" : qUnion([Q0, Q1, Q2, Q3, Q4, Q5]), "radius" : 3 * mm, "tangentPropagation" : true, "allowEdgeOverflow" : false});
        }
        {
            var Q0;
            Q0=makeQuery(id+"F1.opExtrude","CAP_EDGE",EDGE,{"disambiguationData":[OSD([sQuery(id+"F0.wireOp",EDGE,"E1.bottom")])],"isStart":false});
            fillet(context, id + "F15", {"entities" : qUnion([Q0]), "radius" : 2 * mm, "tangentPropagation" : true, "allowEdgeOverflow" : false});
        }
        {
            var Q0;
            {var subQ0=sQuery(id+"F0.wireOp",EDGE,"E21.filletArc");var subQ1=sQuery(id+"F0.wireOp",EDGE,"E7");var subQ2=sQuery(id+"F0.wireOp",EDGE,"E6");var subQ3=sQuery(id+"F0.wireOp",EDGE,"E5");var subQ4=sQuery(id+"F0.wireOp",EDGE,"E4");var subQ5=sQuery(id+"F0.wireOp",EDGE,"E22.filletArc");var subQ6=sQuery(id+"F0.wireOp",EDGE,"E1.bottom");var subQ7=sQuery(id+"F0.wireOp",EDGE,"E1.right");var subQ8=sQuery(id+"F0.wireOp",EDGE,"E1.top");var subQ9=sQuery(id+"F0.wireOp",EDGE,"E1.left");var subQ10=sQuery(id+"F0.wireOp",EDGE,"E23.filletArc");var subQ11=sQuery(id+"F0.wireOp",EDGE,"E24.filletArc");Q0=makeQuery(id+"F2.boolean.opBoolean","SPLIT",FACE,{"disambiguationData":[TD([makeQuery(id+"F1.opExtrude","SWEPT_FACE",FACE,{"disambiguationData":[OSD([subQ6])]})])],"derivedFrom":makeQuery(id+"F1.opExtrude","CAP_FACE",FACE,{"disambiguationData":[OSD([subQ6,subQ8,subQ9,subQ7,subQ4,subQ3,subQ2,subQ1,subQ0,subQ5,subQ10,subQ11])],"isStart":true})});}
            var sketch = newSketch(context, id + "F16", { "sketchPlane" : qUnion([Q0])});
            skLineSegment(sketch, "E79", {"start": v(-32.22, 74.25) * mm, "end": v(-14.22, 92.25) * mm});
            skLineSegment(sketch, "E80", {"start": v(33.77, 74.25) * mm, "end": v(15.77, 92.25) * mm});
            skLineSegment(sketch, "E81", {"start": v(15.77, 92.25) * mm, "end": v(15.77, 104.62) * mm});
            skLineSegment(sketch, "E82", {"start": v(-14.22, 92.25) * mm, "end": v(-14.22, 104.25) * mm});
            skArc(sketch, "E83", {"start": v(15.77, 104.62) * mm, "mid": v(0.6, 119.25) * mm, "end": v(-14.22, 104.25) * mm});
            skCircle(sketch, "E84", {"center": v(0.78, 104.25) * mm, "radius": 6 * mm});
            skLineSegment(sketch, "E85", {"start": v(0.78, 104.25) * mm, "end": v(0.78, 74.25) * mm, "construction": true});
            skLineSegment(sketch, "E86", {"start": v(-74.25, 0) * mm, "end": v(74.25, 0) * mm, "construction": true});
            skLineSegment(sketch, "E87.MirrorCS", {"start": v(-32.22, -74.25) * mm, "end": v(-14.22, -92.25) * mm});
            skLineSegment(sketch, "E88.MirrorCS", {"start": v(-14.22, -92.25) * mm, "end": v(-14.22, -104.25) * mm});
            skLineSegment(sketch, "E89.MirrorCS", {"start": v(0.78, -104.25) * mm, "end": v(0.78, -74.25) * mm, "construction": true});
            skCircle(sketch, "E90.MirrorC", {"center": v(0.78, -104.25) * mm, "radius": 6 * mm});
            skLineSegment(sketch, "E91.MirrorCS", {"start": v(33.77, -74.25) * mm, "end": v(15.77, -92.25) * mm});
            skLineSegment(sketch, "E92.MirrorCS", {"start": v(15.77, -92.25) * mm, "end": v(15.77, -104.62) * mm});
            skArc(sketch, "E93.MirrorCS", {"start": v(15.77, -104.62) * mm, "mid": v(0.6, -119.25) * mm, "end": v(-14.22, -104.25) * mm});
            skSolve(sketch);
        }
        {
            var Q0;
            {var subQ0=sQuery(id+"F16.wireOp",EDGE,"E79");Q0=makeQuery(id+"F16.imprint","IMPRINT",FACE,{"disambiguationData":[TD([[makeQuery(id+"F16.imprint","IMPRINT",EDGE,{"derivedFrom":subQ0}),-1.0]])]});}
            var Q1;
            {var subQ1=sQuery(id+"F16.wireOp",EDGE,"E87.MirrorCS");Q1=makeQuery(id+"F16.imprint","IMPRINT",FACE,{"disambiguationData":[TD([[makeQuery(id+"F16.imprint","IMPRINT",EDGE,{"derivedFrom":subQ1}),1.0]])]});}
            var Q2;
            Q2=makeQuery(id+"F16.imprint","IMPRINT",FACE,{"disambiguationData":[TD([[makeQuery(id+"F16.imprint","IMPRINT",EDGE,{"derivedFrom":makeQuery(id+"F1.opExtrude","CAP_EDGE",EDGE,{"disambiguationData":[OSD([sQuery(id+"F0.wireOp",EDGE,"E1.left")])],"isStart":true})}),-1.0]])]});
            extrude(context, id + "F17", {"entities" : qUnion([Q0, Q1, Q2]), "depth" : 3 * mm});
        }
    });
